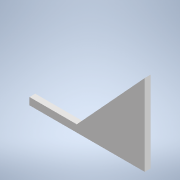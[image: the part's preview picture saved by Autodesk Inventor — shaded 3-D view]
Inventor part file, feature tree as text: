
AUTODESK INVENTOR PART (.ipt)
format: ipt  version: 2021 (Build 250183000, 183)  size: 94,208 bytes
history: native  units: in
note: dims shown in document units (in); Inventor stores cm internally (conversion verified against a paired STEP export)
features: extrude x1, sketch x1
ambient origin geometry x8: Origin, YZ Plane, XZ Plane, XY Plane, X Axis, Y Axis, Z Axis, Center Point
bodies: Solid1 (feature_tree)
feature tree (2):
  extrude  "Extrusion1"  Depth=0.5in TaperAngle=0.0deg
  sketch  "Sketch1"  dims[d2=8.6614in d3=0.5in d4=0.0in]
